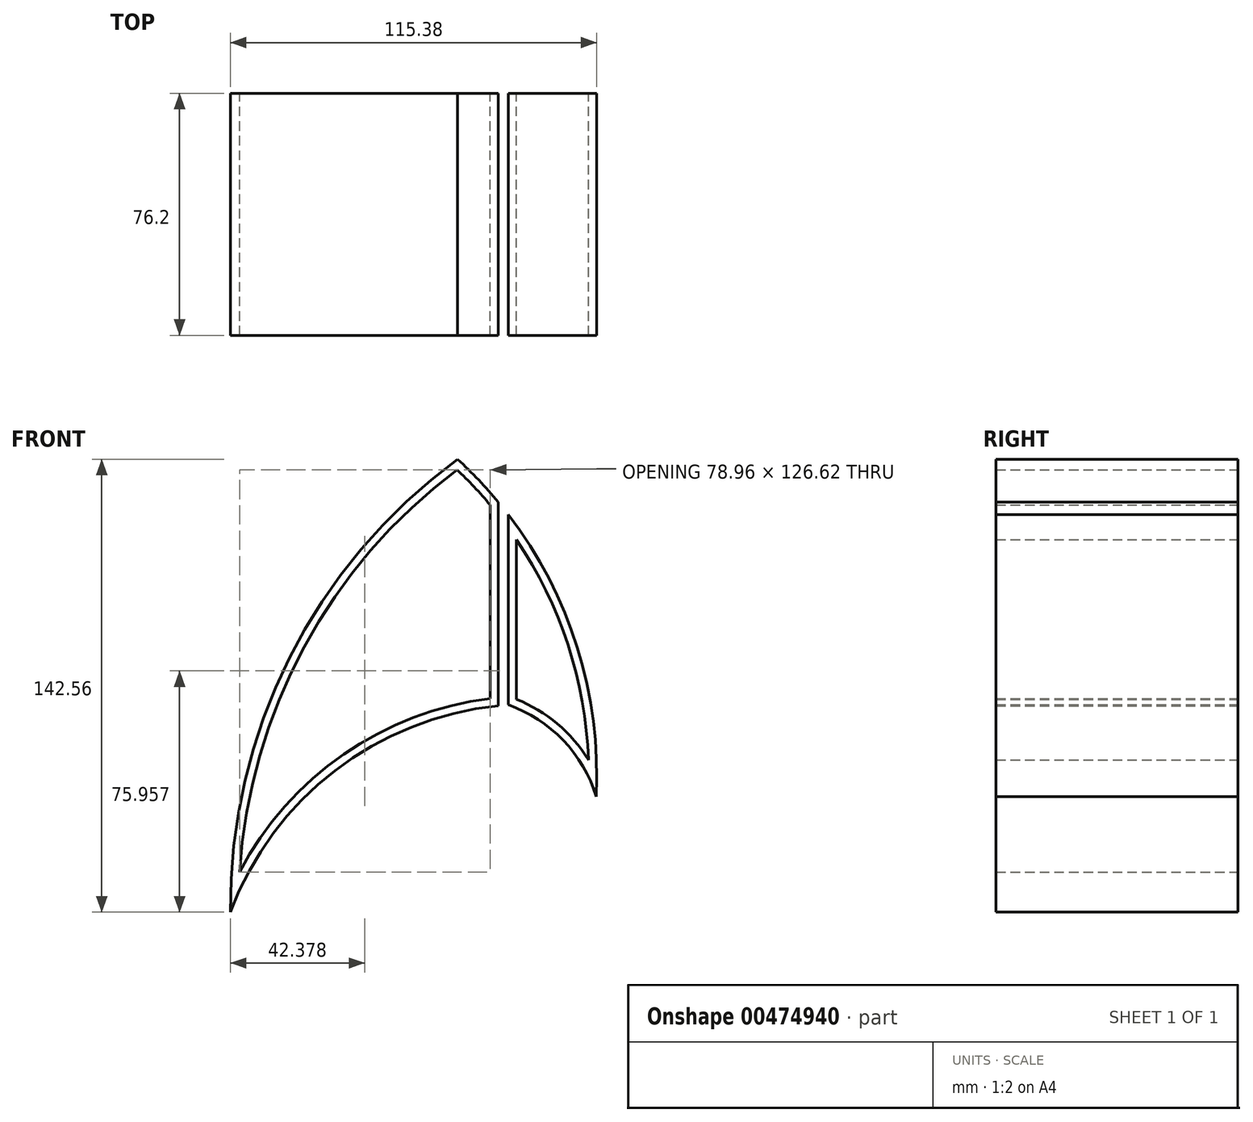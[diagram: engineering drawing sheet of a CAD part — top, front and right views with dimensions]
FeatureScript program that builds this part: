
annotation { "Feature Type Name" : "Feature", "Feature Type Description" : "" }
export const myFeature = defineFeature(function(context is Context, id is Id, definition is map)
    precondition{}
    {
        {
            var Q0;
            Q0=qCreatedBy(makeId("Front.planeOp"),FACE);
            var sketch = newSketch(context, id + "F0", { "sketchPlane" : qUnion([Q0])});
            skArc(sketch, "E0", {"start": v(-12.7, 72.18) * mm, "mid": v(-65.68, 9.54) * mm, "end": v(-84.22, -70.38) * mm});
            skArc(sketch, "E1", {"start": v(30.98, -33.99) * mm, "mid": v(25.04, 12.84) * mm, "end": v(3.3, 54.74) * mm});
            skArc(sketch, "E2", {"start": v(30.98, -33.99) * mm, "mid": v(20.57, -16.27) * mm, "end": v(3.3, -5.11) * mm});
            skArc(sketch, "E3", {"start": v(0.17, -5.38) * mm, "mid": v(-51.3, -25.85) * mm, "end": v(-84.22, -70.38) * mm});
            skLineSegment(sketch, "E4", {"start": v(0.17, -5.38) * mm, "end": v(0.17, 58.68) * mm});
            skLineSegment(sketch, "E5", {"start": v(3.3, 54.74) * mm, "end": v(3.3, -5.11) * mm});
            skArc(sketch, "E6.trimOffspring", {"start": v(0.17, 58.68) * mm, "mid": v(-6.03, 65.65) * mm, "end": v(-12.7, 72.18) * mm});
            skArc(sketch, "E7.0", {"start": v(28.52, -22.43) * mm, "mid": v(22.06, 13.82) * mm, "end": v(5.85, 46.88) * mm});
            skArc(sketch, "E7.1", {"start": v(28.52, -22.43) * mm, "mid": v(18.72, -11.06) * mm, "end": v(5.85, -3.36) * mm});
            skLineSegment(sketch, "E7.2", {"start": v(5.85, 46.88) * mm, "end": v(5.85, -3.36) * mm});
            skArc(sketch, "E8.0", {"start": v(-12.88, 68.89) * mm, "mid": v(-60.97, 13.08) * mm, "end": v(-81.33, -57.73) * mm});
            skArc(sketch, "E8.1", {"start": v(-2.37, 57.76) * mm, "mid": v(-7.46, 63.47) * mm, "end": v(-12.88, 68.89) * mm});
            skLineSegment(sketch, "E8.2", {"start": v(-2.37, -3.11) * mm, "end": v(-2.37, 57.76) * mm});
            skArc(sketch, "E8.3", {"start": v(-2.37, -3.11) * mm, "mid": v(-48.57, -20.71) * mm, "end": v(-81.33, -57.73) * mm});
            skSolve(sketch);
        }
        {
            var Q0;
            Q0=makeQuery(id+"F0.imprint","IMPRINT",FACE,{"disambiguationData":[TD([[makeQuery(id+"F0.imprint","IMPRINT",EDGE,{"derivedFrom":sQuery(id+"F0.wireOp",EDGE,"E0")}),1.0]])]});
            var Q1;
            Q1=makeQuery(id+"F0.imprint","IMPRINT",FACE,{"disambiguationData":[TD([[makeQuery(id+"F0.imprint","IMPRINT",EDGE,{"derivedFrom":sQuery(id+"F0.wireOp",EDGE,"E1")}),1.0]])]});
            extrude(context, id + "F1", {"entities" : qUnion([Q0, Q1]), "depth" : 76.2 * mm});
        }
    });
